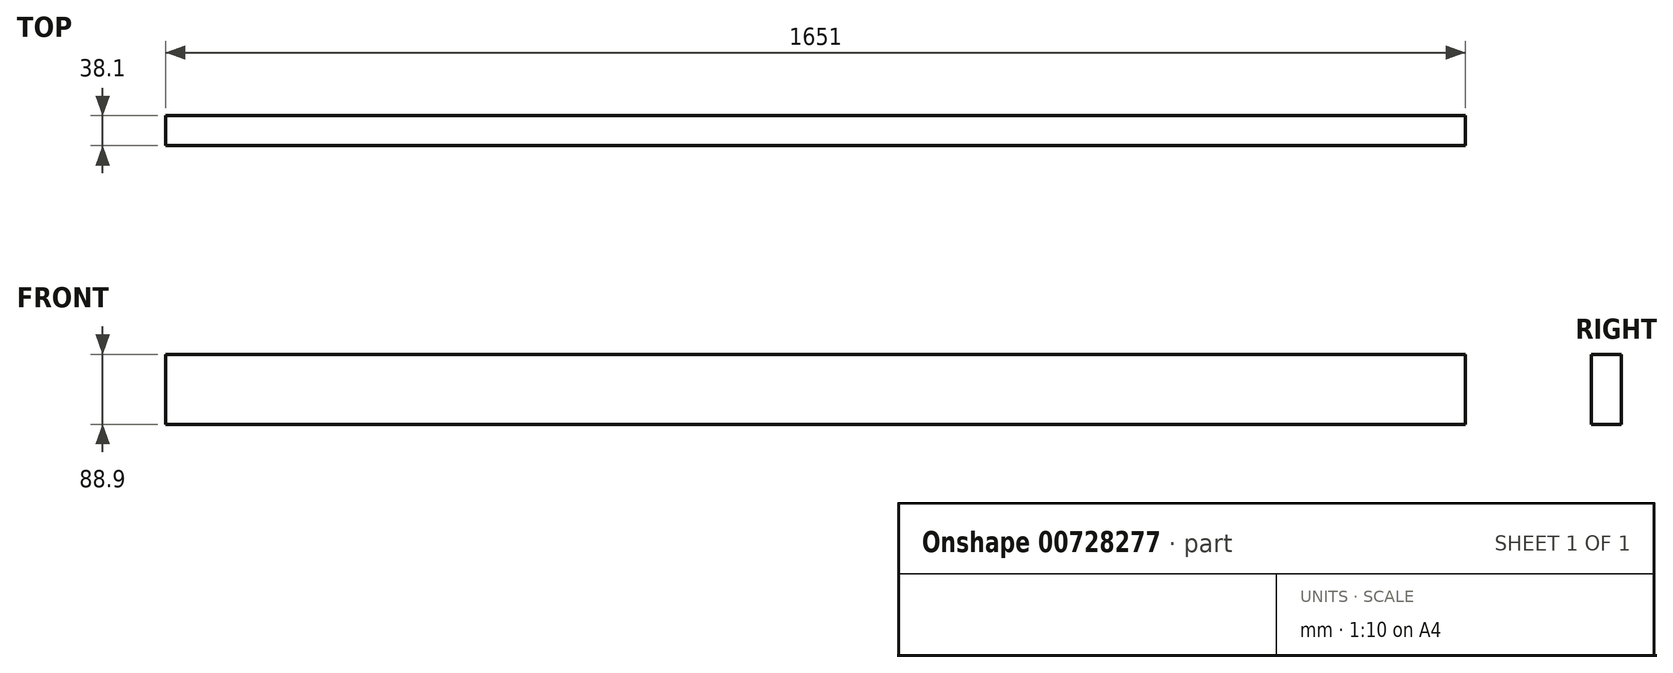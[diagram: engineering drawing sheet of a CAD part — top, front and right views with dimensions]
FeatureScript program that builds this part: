
annotation { "Feature Type Name" : "Feature", "Feature Type Description" : "" }
export const myFeature = defineFeature(function(context is Context, id is Id, definition is map)
    precondition{}
    {
        {
            var Q0;
            Q0=qCreatedBy(makeId("Front.planeOp"),FACE);
            var sketch = newSketch(context, id + "F0", { "sketchPlane" : qUnion([Q0])});
            skLineSegment(sketch, "E0.bottom", {"start": v(-825.5, -44.45) * mm, "end": v(825.5, -44.45) * mm});
            skLineSegment(sketch, "E0.top", {"start": v(-825.5, 44.45) * mm, "end": v(825.5, 44.45) * mm});
            skLineSegment(sketch, "E0.left", {"start": v(-825.5, -44.45) * mm, "end": v(-825.5, 44.45) * mm});
            skLineSegment(sketch, "E0.right", {"start": v(825.5, -44.45) * mm, "end": v(825.5, 44.45) * mm});
            skPoint(sketch, "E0.middle", {"position": v(0, 0) * mm});
            skSolve(sketch);
        }
        {
            var Q0;
            Q0=qSketchRegion(id+"F0",true);
            extrude(context, id + "F1", {"entities" : qUnion([Q0]), "depth" : 38.1 * mm, "offsetDistance" : 25.4 * mm});
        }
    });
